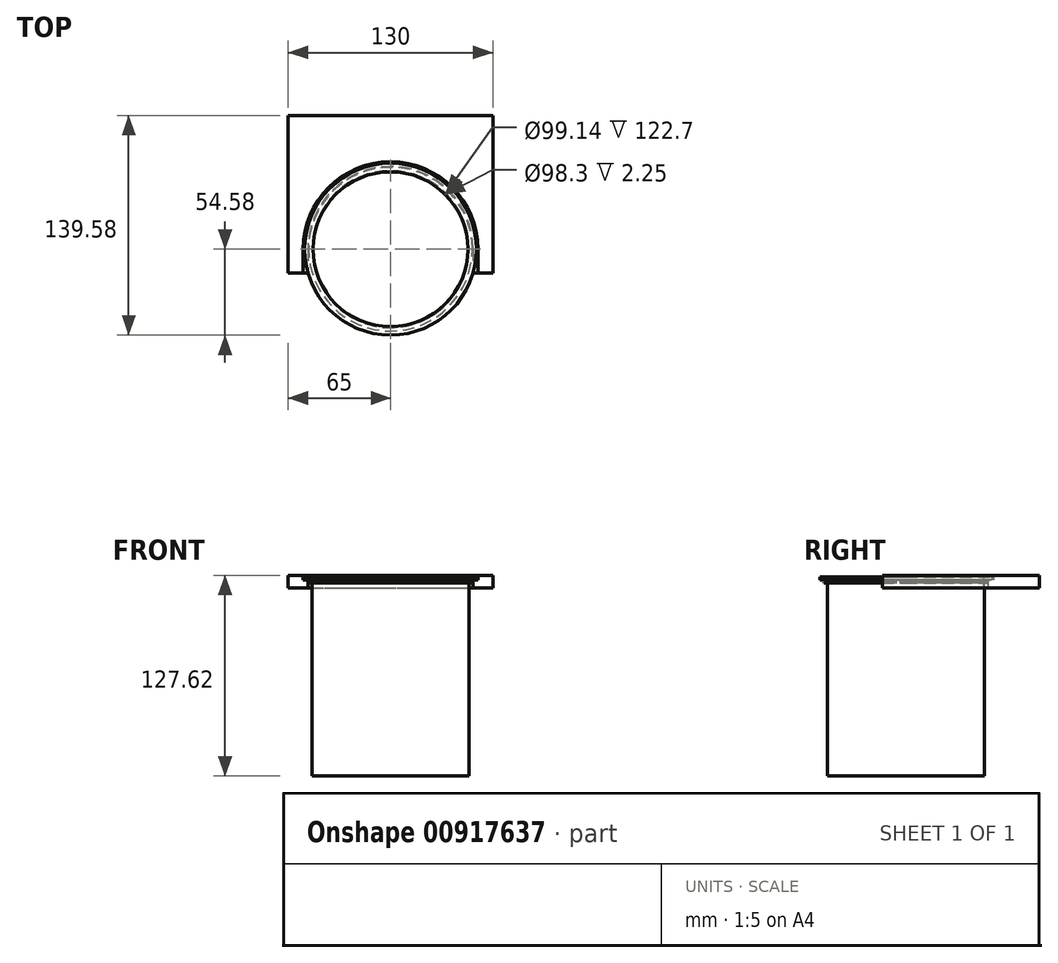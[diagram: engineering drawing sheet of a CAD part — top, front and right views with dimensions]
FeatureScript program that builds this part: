
annotation { "Feature Type Name" : "Feature", "Feature Type Description" : "" }
export const myFeature = defineFeature(function(context is Context, id is Id, definition is map)
    precondition{}
    {
        {
            var Q0;
            Q0=qCreatedBy(makeId("Front.planeOp"),FACE);
            var sketch = newSketch(context, id + "F0", { "sketchPlane" : qUnion([Q0])});
            skLineSegment(sketch, "E0", {"start": v(0, 0) * mm, "end": v(0, 50.36) * mm, "construction": true});
            skLineSegment(sketch, "E1", {"start": v(0, 0) * mm, "end": v(-49.58, 0) * mm});
            skLineSegment(sketch, "E2", {"start": v(-49.58, 0) * mm, "end": v(-49.58, 1.62) * mm});
            skLineSegment(sketch, "E3", {"start": v(-49.58, 1.62) * mm, "end": v(-54.58, 1.62) * mm});
            skLineSegment(sketch, "E4", {"start": v(-54.58, 1.62) * mm, "end": v(-54.58, 3.62) * mm});
            skLineSegment(sketch, "E5", {"start": v(-54.58, 3.62) * mm, "end": v(-49.15, 3.62) * mm});
            skLineSegment(sketch, "E6", {"start": v(-49.15, 3.62) * mm, "end": v(-49.15, 1.37) * mm});
            skLineSegment(sketch, "E7", {"start": v(-49.15, 1.37) * mm, "end": v(0, 1.37) * mm});
            skLineSegment(sketch, "E8", {"start": v(0, 1.37) * mm, "end": v(0, 0) * mm});
            skSolve(sketch);
        }
        {
            var Q0;
            Q0 = qSketchRegion(id + "F0", true);
            var Q1;
            Q1=sQuery(id+"F0.wireOp",EDGE,"E0");
            revolve(context, id + "F1", {"surfaceOperationType" : NewSurfaceOperationType.NEW, "entities" : qUnion([Q0]), "axis" : qUnion([Q1]), "revolveType" : RevolveType.FULL});
        }
        {
            var Q0;
            Q0=qCreatedBy(makeId("Front.planeOp"),FACE);
            var sketch = newSketch(context, id + "F2", { "sketchPlane" : qUnion([Q0])});
            skLineSegment(sketch, "E9", {"start": v(0, 0) * mm, "end": v(0, -123) * mm, "construction": true});
            skLineSegment(sketch, "E10", {"start": v(0, -123) * mm, "end": v(-49.87, -123) * mm});
            skLineSegment(sketch, "E11", {"start": v(-49.87, -123) * mm, "end": v(-49.87, -0.3) * mm});
            skLineSegment(sketch, "E12", {"start": v(-49.87, -0.3) * mm, "end": v(-52, -0.3) * mm});
            skLineSegment(sketch, "E13", {"start": v(-52, -0.3) * mm, "end": v(-52, 0) * mm});
            skLineSegment(sketch, "E14", {"start": v(-52, 0) * mm, "end": v(-49.57, 0) * mm});
            skLineSegment(sketch, "E15", {"start": v(-49.57, 0) * mm, "end": v(-49.57, -122.7) * mm});
            skLineSegment(sketch, "E16", {"start": v(-49.57, -122.7) * mm, "end": v(0, -122.7) * mm});
            skLineSegment(sketch, "E17", {"start": v(0, -122.7) * mm, "end": v(0, -123) * mm});
            skSolve(sketch);
        }
        {
            var Q0;
            Q0 = qSketchRegion(id + "F2", true);
            var Q1;
            Q1=sQuery(id+"F2.wireOp",EDGE,"E9");
            revolve(context, id + "F3", {"surfaceOperationType" : NewSurfaceOperationType.NEW, "entities" : qUnion([Q0]), "axis" : qUnion([Q1]), "revolveType" : RevolveType.FULL});
        }
        {
            var Q0;
            Q0=makeQuery(id+"F1.opRevolve","SWEPT_FACE",FACE,{"disambiguationData":[OSD([sQuery(id+"F0.wireOp",EDGE,"E3")])]});
            var sketch = newSketch(context, id + "F4", { "sketchPlane" : qUnion([Q0])});
            skArc(sketch, "E18", {"start": v(-52.5, 0) * mm, "mid": v(0, -52.5) * mm, "end": v(52.5, 0) * mm});
            skLineSegment(sketch, "E19", {"start": v(-52.5, 0) * mm, "end": v(-52.5, 15) * mm});
            skLineSegment(sketch, "E20", {"start": v(-52.5, 15) * mm, "end": v(-65, 15) * mm});
            skLineSegment(sketch, "E21", {"start": v(-65, 15) * mm, "end": v(-65, -85) * mm});
            skLineSegment(sketch, "E22", {"start": v(-65, -85) * mm, "end": v(65, -85) * mm});
            skLineSegment(sketch, "E23", {"start": v(65, -85) * mm, "end": v(65, 15) * mm});
            skLineSegment(sketch, "E24", {"start": v(65, 15) * mm, "end": v(52.5, 15) * mm});
            skLineSegment(sketch, "E25", {"start": v(52.5, 0) * mm, "end": v(52.5, 15) * mm});
            skSolve(sketch);
        }
        {
            var Q0;
            Q0 = qSketchRegion(id + "F4", true);
            extrude(context, id + "F5", {"entities" : qUnion([Q0]), "depth" : 5 * mm, "offsetDistance" : 25 * mm});
        }
        {
            var Q0;
            Q0=makeQuery(id+"F5.opExtrude","CAP_FACE",FACE,{"disambiguationData":[OSD([sQuery(id+"F4.wireOp",EDGE,"E18"),sQuery(id+"F4.wireOp",EDGE,"E19"),sQuery(id+"F4.wireOp",EDGE,"E20"),sQuery(id+"F4.wireOp",EDGE,"E21"),sQuery(id+"F4.wireOp",EDGE,"E22"),sQuery(id+"F4.wireOp",EDGE,"E23"),sQuery(id+"F4.wireOp",EDGE,"E24"),sQuery(id+"F4.wireOp",EDGE,"E25")])],"isStart":true});
            var sketch = newSketch(context, id + "F6", { "sketchPlane" : qUnion([Q0])});
            skArc(sketch, "E26", {"start": v(55.5, 0) * mm, "mid": v(0, 55.5) * mm, "end": v(-55.5, 0) * mm});
            skPoint(sketch, "E27.endSnap0", {"position": v(58.75, -15) * mm});
            skLineSegment(sketch, "E28", {"start": v(-55.5, 0) * mm, "end": v(-55.5, -15) * mm});
            skLineSegment(sketch, "E29", {"start": v(55.5, 0) * mm, "end": v(55.5, -15) * mm});
            skLineSegment(sketch, "E30", {"start": v(55.5, -15) * mm, "end": v(65, -15) * mm});
            skLineSegment(sketch, "E31", {"start": v(65, -15) * mm, "end": v(65, 85) * mm});
            skLineSegment(sketch, "E32", {"start": v(65, 85) * mm, "end": v(-65, 85) * mm});
            skLineSegment(sketch, "E33", {"start": v(-65, 85) * mm, "end": v(-65, -15) * mm});
            skLineSegment(sketch, "E34", {"start": v(-65, -15) * mm, "end": v(-55.5, -15) * mm});
            skSolve(sketch);
        }
        {
            var Q0;
            Q0 = qSketchRegion(id + "F6", true);
            extrude(context, id + "F7", {"entities" : qUnion([Q0]), "operationType" : NewBodyOperationType.ADD, "depth" : 3 * mm, "offsetDistance" : 25 * mm});
        }
    });
